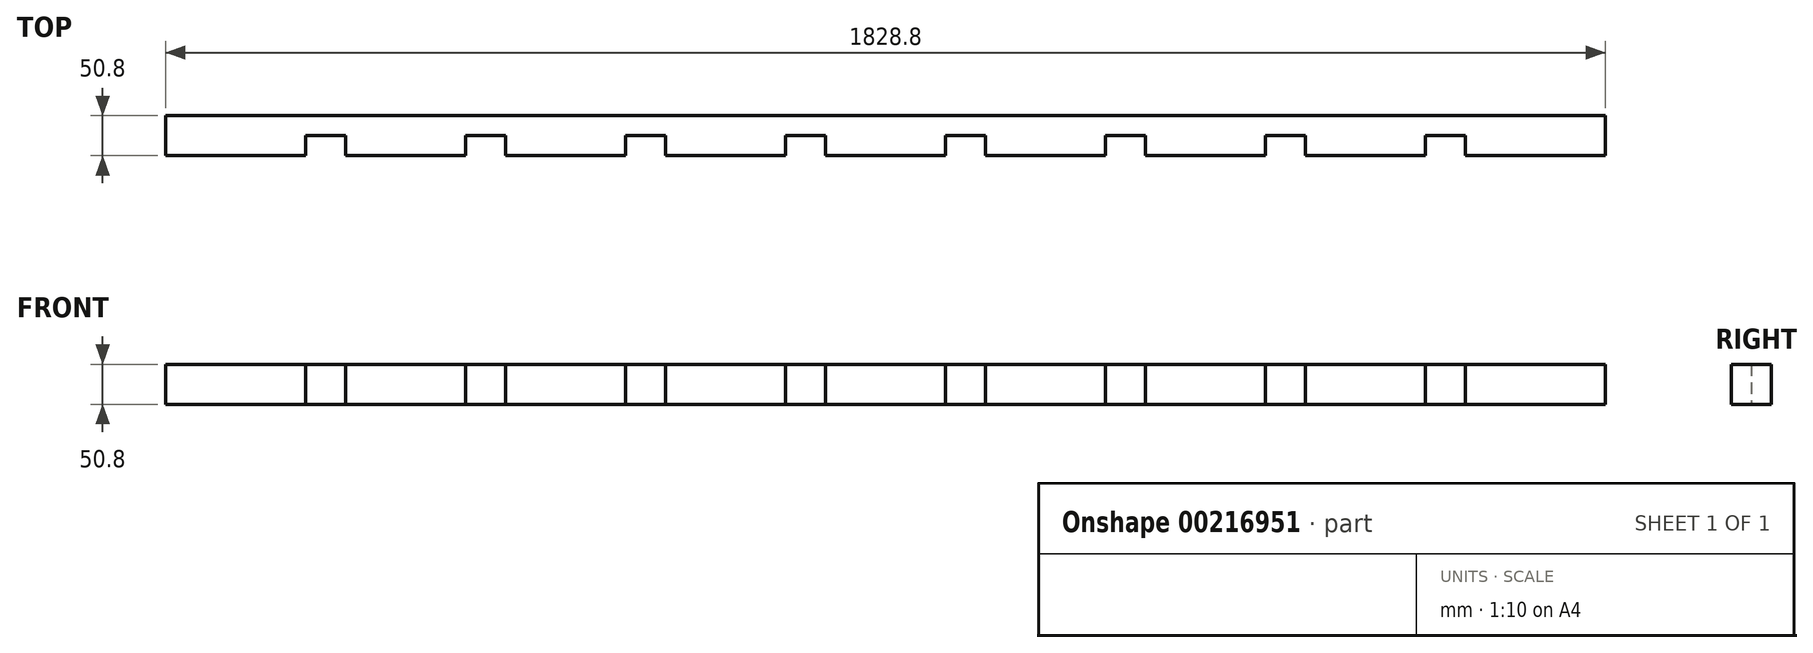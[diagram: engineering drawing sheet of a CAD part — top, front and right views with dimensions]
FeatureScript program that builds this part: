
annotation { "Feature Type Name" : "Feature", "Feature Type Description" : "" }
export const myFeature = defineFeature(function(context is Context, id is Id, definition is map)
    precondition{}
    {
        {
            var Q0;
            Q0=qCreatedBy(makeId("Top.planeOp"),FACE);
            var sketch = newSketch(context, id + "F0", { "sketchPlane" : qUnion([Q0])});
            skLineSegment(sketch, "E0", {"start": v(0, 0) * mm, "end": v(-76.2, 0) * mm});
            skLineSegment(sketch, "E1", {"start": v(-1219.2, 0) * mm, "end": v(-1219.2, 50.8) * mm});
            skLineSegment(sketch, "E2", {"start": v(-1219.2, 50.8) * mm, "end": v(-736.6, 50.8) * mm});
            skLineSegment(sketch, "E3", {"start": v(1219.2, 50.8) * mm, "end": v(1219.2, 0) * mm});
            skLineSegment(sketch, "E4", {"start": v(1219.2, 0) * mm, "end": v(736.6, 0) * mm});
            skLineSegment(sketch, "E5", {"start": v(0, 0) * mm, "end": v(76.2, 0) * mm});
            skLineSegment(sketch, "E6", {"start": v(76.2, 0) * mm, "end": v(76.2, 50.8) * mm});
            skLineSegment(sketch, "E7", {"start": v(127, 50.8) * mm, "end": v(127, 0) * mm});
            skLineSegment(sketch, "E8", {"start": v(127, 0) * mm, "end": v(279.4, 0) * mm});
            skLineSegment(sketch, "E9", {"start": v(279.4, 0) * mm, "end": v(279.4, 50.8) * mm});
            skLineSegment(sketch, "E10", {"start": v(330.2, 50.8) * mm, "end": v(330.2, 0) * mm});
            skLineSegment(sketch, "E11", {"start": v(330.2, 0) * mm, "end": v(482.6, 0) * mm});
            skLineSegment(sketch, "E12", {"start": v(482.6, 0) * mm, "end": v(482.6, 50.8) * mm});
            skLineSegment(sketch, "E13", {"start": v(533.4, 50.8) * mm, "end": v(533.4, 0) * mm});
            skLineSegment(sketch, "E14", {"start": v(533.4, 0) * mm, "end": v(685.8, 0) * mm});
            skLineSegment(sketch, "E15", {"start": v(685.8, 0) * mm, "end": v(685.8, 50.8) * mm});
            skLineSegment(sketch, "E16", {"start": v(736.6, 50.8) * mm, "end": v(736.6, 0) * mm});
            skLineSegment(sketch, "E17", {"start": v(-76.2, 0) * mm, "end": v(-76.2, 50.8) * mm});
            skLineSegment(sketch, "E18", {"start": v(-127, 50.8) * mm, "end": v(-279.4, 50.8) * mm});
            skLineSegment(sketch, "E19", {"start": v(-279.4, 50.8) * mm, "end": v(-279.4, 0) * mm});
            skLineSegment(sketch, "E20", {"start": v(-330.2, 0) * mm, "end": v(-330.2, 50.8) * mm});
            skLineSegment(sketch, "E21", {"start": v(-330.2, 50.8) * mm, "end": v(-482.6, 50.8) * mm});
            skLineSegment(sketch, "E22", {"start": v(-482.6, 50.8) * mm, "end": v(-482.6, 0) * mm});
            skLineSegment(sketch, "E23", {"start": v(-533.4, 0) * mm, "end": v(-533.4, 50.8) * mm});
            skLineSegment(sketch, "E24", {"start": v(-533.4, 50.8) * mm, "end": v(-685.8, 50.8) * mm});
            skLineSegment(sketch, "E25", {"start": v(-685.8, 50.8) * mm, "end": v(-685.8, 0) * mm});
            skLineSegment(sketch, "E26", {"start": v(-736.6, 0) * mm, "end": v(-736.6, 50.8) * mm});
            skLineSegment(sketch, "E27", {"start": v(-127, 0) * mm, "end": v(-127, 50.8) * mm});
            skLineSegment(sketch, "E28.trimOffspring", {"start": v(-685.8, 50.8) * mm, "end": v(-533.4, 50.8) * mm});
            skLineSegment(sketch, "E29.trimOffspring", {"start": v(-482.6, 50.8) * mm, "end": v(-330.2, 50.8) * mm});
            skLineSegment(sketch, "E30.trimOffspring", {"start": v(-279.4, 50.8) * mm, "end": v(-127, 50.8) * mm});
            skLineSegment(sketch, "E31.trimOffspring", {"start": v(-736.6, 0) * mm, "end": v(-1219.2, 0) * mm});
            skLineSegment(sketch, "E32.trimOffspring", {"start": v(-533.4, 0) * mm, "end": v(-685.8, 0) * mm});
            skLineSegment(sketch, "E33.trimOffspring", {"start": v(-330.2, 0) * mm, "end": v(-482.6, 0) * mm});
            skLineSegment(sketch, "E34.trimOffspring", {"start": v(-127, 0) * mm, "end": v(-279.4, 0) * mm});
            skLineSegment(sketch, "E35.trimOffspring", {"start": v(-76.2, 50.8) * mm, "end": v(76.2, 50.8) * mm});
            skLineSegment(sketch, "E36.trimOffspring", {"start": v(76.2, 0) * mm, "end": v(0, 0) * mm});
            skLineSegment(sketch, "E37.trimOffspring", {"start": v(127, 50.8) * mm, "end": v(279.4, 50.8) * mm});
            skLineSegment(sketch, "E38.trimOffspring", {"start": v(279.4, 0) * mm, "end": v(127, 0) * mm});
            skLineSegment(sketch, "E39.trimOffspring", {"start": v(330.2, 50.8) * mm, "end": v(482.6, 50.8) * mm});
            skLineSegment(sketch, "E40.trimOffspring", {"start": v(482.6, 0) * mm, "end": v(330.2, 0) * mm});
            skLineSegment(sketch, "E41.trimOffspring", {"start": v(533.4, 50.8) * mm, "end": v(685.8, 50.8) * mm});
            skLineSegment(sketch, "E42.trimOffspring", {"start": v(685.8, 0) * mm, "end": v(533.4, 0) * mm});
            skLineSegment(sketch, "E43.trimOffspring", {"start": v(736.6, 50.8) * mm, "end": v(1219.2, 50.8) * mm});
            skSolve(sketch);
        }
        {
            var Q0;
            Q0 = qSketchRegion(id + "F0", true);
            extrude(context, id + "F1", {"entities" : qUnion([Q0]), "depth" : 25.4 * mm});
        }
        {
            var Q0;
            Q0=makeQuery(id+"F1.opExtrude","CAP_FACE",FACE,{"disambiguationData":[OSD([sQuery(id+"F0.wireOp",EDGE,"E6"),sQuery(id+"F0.wireOp",EDGE,"E0"),sQuery(id+"F0.wireOp",EDGE,"E17"),sQuery(id+"F0.wireOp",EDGE,"E35.trimOffspring"),sQuery(id+"F0.wireOp",EDGE,"E36.trimOffspring")])],"isStart":false});
            var sketch = newSketch(context, id + "F2", { "sketchPlane" : qUnion([Q0])});
            skLineSegment(sketch, "E44.bottom", {"start": v(-1219.2, 0) * mm, "end": v(1219.2, 0) * mm});
            skLineSegment(sketch, "E44.top", {"start": v(-1219.2, 50.8) * mm, "end": v(1219.2, 50.8) * mm});
            skLineSegment(sketch, "E44.left", {"start": v(-1219.2, 0) * mm, "end": v(-1219.2, 50.8) * mm});
            skLineSegment(sketch, "E44.right", {"start": v(1219.2, 0) * mm, "end": v(1219.2, 50.8) * mm});
            skPoint(sketch, "E44.middle", {"position": v(0, 25.4) * mm});
            skPoint(sketch, "E44.middle.positionSnap0", {"position": v(76.2, 25.4) * mm});
            skPoint(sketch, "E44.middle.positionSnap1", {"position": v(0, 50.8) * mm});
            skPoint(sketch, "E44.cornerSnap0", {"position": v(0, 0) * mm});
            skPoint(sketch, "E44.centerSnap0", {"position": v(76.2, 25.4) * mm});
            skPoint(sketch, "E44.centerSnap1", {"position": v(0, 50.8) * mm});
            skSolve(sketch);
        }
        {
            var Q0;
            Q0 = qSketchRegion(id + "F2", true);
            extrude(context, id + "F3", {"entities" : qUnion([Q0]), "depth" : 25.4 * mm});
        }
        {
            var Q0;
            Q0=makeQuery(id+"F1.opExtrude","SWEPT_BODY",BODY,{"disambiguationData":[OSD([sQuery(id+"F0.wireOp",EDGE,"E1"),sQuery(id+"F0.wireOp",EDGE,"E2"),sQuery(id+"F0.wireOp",EDGE,"E26"),sQuery(id+"F0.wireOp",EDGE,"E31.trimOffspring")])]});
            var Q1;
            Q1=makeQuery(id+"F1.opExtrude","SWEPT_BODY",BODY,{"disambiguationData":[OSD([sQuery(id+"F0.wireOp",EDGE,"E3"),sQuery(id+"F0.wireOp",EDGE,"E4"),sQuery(id+"F0.wireOp",EDGE,"E16"),sQuery(id+"F0.wireOp",EDGE,"E43.trimOffspring")])]});
            var Q2;
            Q2=makeQuery(id+"F1.opExtrude","SWEPT_BODY",BODY,{"disambiguationData":[OSD([sQuery(id+"F0.wireOp",EDGE,"E6"),sQuery(id+"F0.wireOp",EDGE,"E0"),sQuery(id+"F0.wireOp",EDGE,"E17"),sQuery(id+"F0.wireOp",EDGE,"E35.trimOffspring"),sQuery(id+"F0.wireOp",EDGE,"E36.trimOffspring")])]});
            var Q3;
            Q3=makeQuery(id+"F1.opExtrude","SWEPT_BODY",BODY,{"disambiguationData":[OSD([sQuery(id+"F0.wireOp",EDGE,"E7"),sQuery(id+"F0.wireOp",EDGE,"E9"),sQuery(id+"F0.wireOp",EDGE,"E37.trimOffspring"),sQuery(id+"F0.wireOp",EDGE,"E38.trimOffspring")])]});
            var Q4;
            Q4=makeQuery(id+"F1.opExtrude","SWEPT_BODY",BODY,{"disambiguationData":[OSD([sQuery(id+"F0.wireOp",EDGE,"E10"),sQuery(id+"F0.wireOp",EDGE,"E12"),sQuery(id+"F0.wireOp",EDGE,"E39.trimOffspring"),sQuery(id+"F0.wireOp",EDGE,"E40.trimOffspring")])]});
            var Q5;
            Q5=makeQuery(id+"F1.opExtrude","SWEPT_BODY",BODY,{"disambiguationData":[OSD([sQuery(id+"F0.wireOp",EDGE,"E13"),sQuery(id+"F0.wireOp",EDGE,"E15"),sQuery(id+"F0.wireOp",EDGE,"E41.trimOffspring"),sQuery(id+"F0.wireOp",EDGE,"E42.trimOffspring")])]});
            var Q6;
            Q6=makeQuery(id+"F1.opExtrude","SWEPT_BODY",BODY,{"disambiguationData":[OSD([sQuery(id+"F0.wireOp",EDGE,"E19"),sQuery(id+"F0.wireOp",EDGE,"E27"),sQuery(id+"F0.wireOp",EDGE,"E30.trimOffspring"),sQuery(id+"F0.wireOp",EDGE,"E34.trimOffspring")])]});
            var Q7;
            Q7=makeQuery(id+"F1.opExtrude","SWEPT_BODY",BODY,{"disambiguationData":[OSD([sQuery(id+"F0.wireOp",EDGE,"E20"),sQuery(id+"F0.wireOp",EDGE,"E22"),sQuery(id+"F0.wireOp",EDGE,"E29.trimOffspring"),sQuery(id+"F0.wireOp",EDGE,"E33.trimOffspring")])]});
            var Q8;
            Q8=makeQuery(id+"F1.opExtrude","SWEPT_BODY",BODY,{"disambiguationData":[OSD([sQuery(id+"F0.wireOp",EDGE,"E23"),sQuery(id+"F0.wireOp",EDGE,"E25"),sQuery(id+"F0.wireOp",EDGE,"E28.trimOffspring"),sQuery(id+"F0.wireOp",EDGE,"E32.trimOffspring")])]});
            var Q9;
            Q9=makeQuery(id+"F3.opExtrude","SWEPT_BODY",BODY,{"disambiguationData":[OSD([sQuery(id+"F2.wireOp",EDGE,"E44.bottom"),sQuery(id+"F2.wireOp",EDGE,"E44.top"),sQuery(id+"F2.wireOp",EDGE,"E44.left"),sQuery(id+"F2.wireOp",EDGE,"E44.right")])]});
            booleanBodies(context, id + "F4", {"operationType" : BooleanOperationType.UNION, "tools" : qUnion([Q0, Q1, Q2, Q3, Q4, Q5, Q6, Q7, Q8, Q9])});
        }
        {
            var Q0;
            Q0=makeQuery(id+"F4.opBoolean","MERGE",FACE,{"derivedFrom":[makeQuery(id+"F1.opExtrude","SWEPT_FACE",FACE,{"disambiguationData":[OSD([sQuery(id+"F0.wireOp",EDGE,"E4")])]}),makeQuery(id+"F1.opExtrude","SWEPT_FACE",FACE,{"disambiguationData":[OSD([sQuery(id+"F0.wireOp",EDGE,"E0"),sQuery(id+"F0.wireOp",EDGE,"E36.trimOffspring")])]}),makeQuery(id+"F1.opExtrude","SWEPT_FACE",FACE,{"disambiguationData":[OSD([sQuery(id+"F0.wireOp",EDGE,"E31.trimOffspring")])]}),makeQuery(id+"F1.opExtrude","SWEPT_FACE",FACE,{"disambiguationData":[OSD([sQuery(id+"F0.wireOp",EDGE,"E32.trimOffspring")])]}),makeQuery(id+"F1.opExtrude","SWEPT_FACE",FACE,{"disambiguationData":[OSD([sQuery(id+"F0.wireOp",EDGE,"E33.trimOffspring")])]}),makeQuery(id+"F1.opExtrude","SWEPT_FACE",FACE,{"disambiguationData":[OSD([sQuery(id+"F0.wireOp",EDGE,"E34.trimOffspring")])]}),makeQuery(id+"F1.opExtrude","SWEPT_FACE",FACE,{"disambiguationData":[OSD([sQuery(id+"F0.wireOp",EDGE,"E38.trimOffspring")])]}),makeQuery(id+"F1.opExtrude","SWEPT_FACE",FACE,{"disambiguationData":[OSD([sQuery(id+"F0.wireOp",EDGE,"E40.trimOffspring")])]}),makeQuery(id+"F1.opExtrude","SWEPT_FACE",FACE,{"disambiguationData":[OSD([sQuery(id+"F0.wireOp",EDGE,"E42.trimOffspring")])]}),makeQuery(id+"F3.opExtrude","SWEPT_FACE",FACE,{"disambiguationData":[OSD([sQuery(id+"F2.wireOp",EDGE,"E44.bottom")])]})]});
            var sketch = newSketch(context, id + "F5", { "sketchPlane" : qUnion([Q0])});
            skLineSegment(sketch, "E45.bottom", {"start": v(-1219.2, 50.8) * mm, "end": v(-914.4, 50.8) * mm});
            skLineSegment(sketch, "E45.top", {"start": v(-1219.2, 0) * mm, "end": v(-914.4, 0) * mm});
            skLineSegment(sketch, "E45.left", {"start": v(-1219.2, 50.8) * mm, "end": v(-1219.2, 0) * mm});
            skLineSegment(sketch, "E45.right", {"start": v(-914.4, 50.8) * mm, "end": v(-914.4, 0) * mm});
            skLineSegment(sketch, "E46.bottom", {"start": v(1219.2, 50.8) * mm, "end": v(914.4, 50.8) * mm});
            skLineSegment(sketch, "E46.top", {"start": v(1219.2, 0) * mm, "end": v(914.4, 0) * mm});
            skLineSegment(sketch, "E46.left", {"start": v(1219.2, 50.8) * mm, "end": v(1219.2, 0) * mm});
            skLineSegment(sketch, "E46.right", {"start": v(914.4, 50.8) * mm, "end": v(914.4, 0) * mm});
            skSolve(sketch);
        }
        {
            var Q0;
            Q0 = qSketchRegion(id + "F5", true);
            extrude(context, id + "F6", {"entities" : qUnion([Q0]), "operationType" : NewBodyOperationType.REMOVE, "oppositeDirection" : true, "depth" : 63.5 * mm});
        }
        {
            var Q0;
            Q0=makeQuery(id+"F1.opExtrude","SWEPT_BODY",BODY,{"disambiguationData":[OSD([sQuery(id+"F0.wireOp",EDGE,"E1"),sQuery(id+"F0.wireOp",EDGE,"E2"),sQuery(id+"F0.wireOp",EDGE,"E26"),sQuery(id+"F0.wireOp",EDGE,"E31.trimOffspring")])]});
            var Q1;
            Q1=makeQuery(id+"F3.opExtrude","CAP_EDGE",EDGE,{"disambiguationData":[OSD([sQuery(id+"F2.wireOp",EDGE,"E44.bottom")])],"isStart":false});
            transform(context, id + "F7", {"entities" : qUnion([Q0]), "transformType" : TransformType.ROTATION, "transformAxis" : qUnion([Q1]), "angle" : 90 * degree, "oppositeDirection" : true, "makeCopy" : false});
        }
    });
